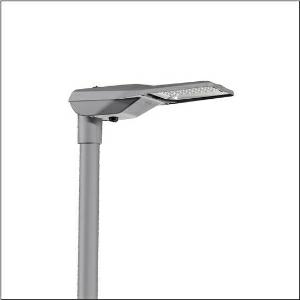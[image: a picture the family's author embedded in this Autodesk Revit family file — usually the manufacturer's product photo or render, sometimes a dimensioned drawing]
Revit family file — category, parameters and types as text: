
# Revit family: streetlight_sl_21_mini___pl52_5xe2h33t08hb_6eb8
name_source: partatom
category: Lighting Fixtures
units: mm (PartAtom-declared; Revit-internal decimal feet)

## family parameters
Cut with Voids When Loaded = No
Host = Face
Light Source = No
Part Type = Normal
Room Calculation Point = No
Round Connector Dimension = Use Diameter
Shared = No

## types (1)
- --- (1 x LED, 8890 lm, 66 W, 3000K)
    Apparent Load = 66 VA
    CIE Flux Codes = 27 59 98 100 100
    Color Rendering = 70
    Color Temperature = 3000K
    Default Elevation = 1800 mm
    Description = Streetlight SL 21 mini, mast luminaire, primary light control with lens, of PMMA, primary optical cover: cover, of toughened safety glass, transparent, light distribution: PL52, light emission: direct distribution, primary light characteristic: asymmetric, installation type: side-entry, post-top, LED, High Power LED, rated luminous flux: 8.890lm, luminous efficacy: 135lm/W, light colour: 730, colour temperature: 3000K, control gear: D4i, control: overheat protection, constant luminous flux control, time-dependent luminous flux control, flexible luminous flux parameterisation, pre-setting: logarithmic dimming characteristic, mains connection: 220..240V, AC, 50/60Hz, start of lifetime: 66W, end of service life: 69W, reduction: 30W, luminaire housing, of diecast aluminium, powder-coated, SITECO metallic grey (DB 702S), corrosivity category C5 high according to DIN EN ISO 12944, please order mast flange separately, inclination adjustable: 0°, 5°, 10°, 15°, sealing non-destructively replaceable, multi-level sealing system, length: 628mm, width: 235mm, height: 110mm, mast flange for spigot size: 42mm (side-entry): 5XC10008XM4, 60/48mm (side-entry/post-top): 5XC10108XM2, 76/60mm (side-entry/post-top): 5XC10108XM1, mounting height: 4..8m, Smart Interface below and above, protection rating (complete): IP66, insulation class (complete): insulation class II (safety insulation), certification: CE, ENEC, ENEC+, VDE, impact resistance: IK10, permissible operating ambient temperature for outdoor applications: -40..+50°C, standard-compliant lighting for roads and squares, packaging unit: 1 piece

Light Distribution: PL52
    Height = 110 mm
    Lamp = 1 x LED
    Lamp Light Flux = 8890 lm
    Lamp Power = 66 W
    Lamp count = 1
    Length = 625 mm
    Luminous efficacy = 135 lm/W
    Manufacturer = Siteco
    ModVariant = No
    Model = 5XE2H33T08HB
    Number of Poles = 1
    OnlyDefault = Yes
    Power Factor = 1
    Product Name = Streetlight SL 21 mini | PL52
    Product group = mast luminaire | pylon top
    ProductGroupID = 6100
    Protection Class = Protection class II
    Protection Degree = IP 66
    RLX_Detail_Level = 1
    RLX_Emergency_Light_Flux = 0 lm
    RLX_Emergency_Type = 0
    RLX_Emergency_Type_DB = No
    RlxData = <blob elided: 35853 chars, md5=b8caba77>
    Socket = socket
    Standby Power = 0 W
    System Light Flux = 8890 lm
    System Power = 66 W
    Type Comments = factory setting: luminous flux: 100 % | dim-lin: 254 | 670 mA
    Type Image = l_1003514.jpg
    URL = http://relux.com
    VarID = @adj_187447
    Voltage = 0 V
    Weight = 0.00 kg
    Width = 234 mm

## geometry (parser evidence)
native form markers: Blend x4, Sweep x12
no freeform markers — native parametric forms only
